# Revit family: Runtal-EB3-120D-120-Volts-96
name_source: partatom
category: Mechanical Equipment
units: mm (PartAtom-declared; Revit-internal decimal feet)

## family parameters
Classification Number = 23.75.10.14.14
Cut with Voids When Loaded = No
Host = Face
Maintain Annotation Orientation = No
Part Type = Normal
Room Calculation Point = No
Round Connector Dimension = Use Diameter
Shared = No

## types (1)
- Radiator-EB3-120D-96-Runtal-Electric Baseboard
    Assembly Code = D3020
    Casing = Powder Coated-Runtal-W-White
    Default Elevation = 4.479 '
    Description = 96" Runtal’s electric baseboard combines high outputs and low surface temperatures with the fine design and outstanding outputs.
    Grille = Yes
    Lamelle = Yes
    Logo = Paint-Runtal-B-Black Matte
    Manufacturer = Runtal Radiators
    Model = EB3-120D-(120 Volts)96
    URL = http://www.runtalnorthamerica.com
    Vertical Conection = Powder Coated-Runtal- Brass

## geometry (parser evidence)
native form markers: Blend x40, Sweep x7
no freeform markers — native parametric forms only
